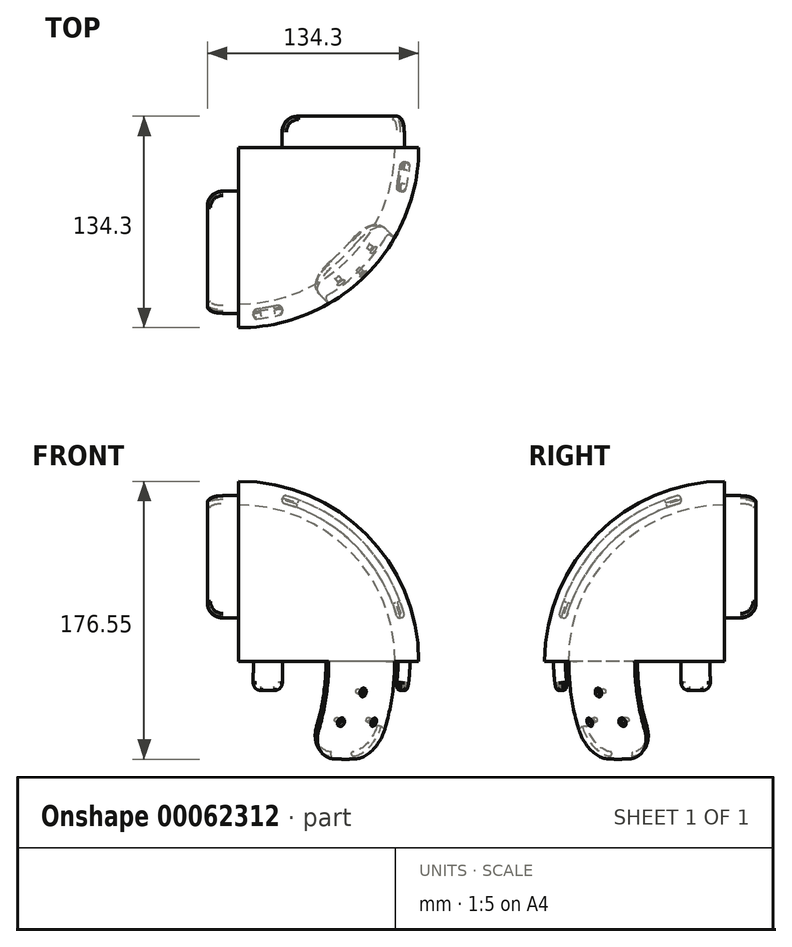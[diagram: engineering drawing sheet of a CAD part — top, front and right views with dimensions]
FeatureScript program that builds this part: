
annotation { "Feature Type Name" : "Feature", "Feature Type Description" : "" }
export const myFeature = defineFeature(function(context is Context, id is Id, definition is map)
    precondition{}
    {
        {
            var Q0;
            Q0=qCreatedBy(makeId("Right.planeOp"),FACE);
            var sketch = newSketch(context, id + "F0", { "sketchPlane" : qUnion([Q0])});
            skArc(sketch, "E0", {"start": v(0, 114.3) * mm, "mid": v(-80.82, 80.82) * mm, "end": v(-114.3, 0) * mm});
            skArc(sketch, "E1", {"start": v(0, 99.3) * mm, "mid": v(-70.22, 70.22) * mm, "end": v(-99.3, 0) * mm});
            skLineSegment(sketch, "E2", {"start": v(0, 99.3) * mm, "end": v(0, 114.3) * mm});
            skLineSegment(sketch, "E3", {"start": v(-99.3, 0) * mm, "end": v(-114.3, 0) * mm});
            skSolve(sketch);
        }
        {
            var Q0;
            Q0=makeQuery(id+"F0.imprint","IMPRINT",FACE,{"disambiguationData":[TD([[makeQuery(id+"F0.imprint","IMPRINT",EDGE,{"derivedFrom":sQuery(id+"F0.wireOp",EDGE,"E0")}),1.0]])]});
            var Q1;
            Q1=sQuery(id+"F0.wireOp",EDGE,"E2");
            revolve(context, id + "F1", {"entities" : qUnion([Q0]), "axis" : qUnion([Q1]), "revolveType" : RevolveType.ONE_DIRECTION, "angle" : 90 * degree});
        }
        {
            var Q0;
            Q0=makeQuery(id+"F1.opRevolve","CAP_FACE",FACE,{"disambiguationData":[OSD([sQuery(id+"F0.wireOp",EDGE,"E0"),sQuery(id+"F0.wireOp",EDGE,"E1"),sQuery(id+"F0.wireOp",EDGE,"E2"),sQuery(id+"F0.wireOp",EDGE,"E3")])],"isStart":false});
            var sketch = newSketch(context, id + "F2", { "sketchPlane" : qUnion([Q0])});
            skArc(sketch, "E4", {"start": v(-28.29, 105.58) * mm, "mid": v(-77.29, 77.29) * mm, "end": v(-105.58, 28.29) * mm});
            skArc(sketch, "E5", {"start": v(-27, 100.75) * mm, "mid": v(-73.75, 73.75) * mm, "end": v(-100.75, 27) * mm});
            skLineSegment(sketch, "E6", {"start": v(-27, 100.75) * mm, "end": v(-28.29, 105.58) * mm});
            skLineSegment(sketch, "E7", {"start": v(-100.75, 27) * mm, "end": v(-105.58, 28.29) * mm});
            skSolve(sketch);
        }
        {
            var Q0;
            Q0=makeQuery(id+"F2.imprint","IMPRINT",FACE,{"disambiguationData":[TD([[makeQuery(id+"F2.imprint","IMPRINT",EDGE,{"derivedFrom":sQuery(id+"F2.wireOp",EDGE,"E4")}),1.0]])]});
            extrude(context, id + "F3", {"entities" : qUnion([Q0]), "operationType" : NewBodyOperationType.ADD, "depth" : 20 * mm});
        }
        {
            var Q0;
            Q0=makeQuery(id+"F0.imprint","IMPRINT",FACE,{"disambiguationData":[TD([[makeQuery(id+"F0.imprint","IMPRINT",EDGE,{"derivedFrom":sQuery(id+"F0.wireOp",EDGE,"E0")}),1.0]])]});
            var sketch = newSketch(context, id + "F4", { "sketchPlane" : qUnion([Q0])});
            skArc(sketch, "E8.0", {"start": v(-27, 100.75) * mm, "mid": v(-73.75, 73.75) * mm, "end": v(-100.75, 27) * mm});
            skArc(sketch, "E9.0", {"start": v(-28.29, 105.58) * mm, "mid": v(-77.29, 77.29) * mm, "end": v(-105.58, 28.29) * mm});
            skLineSegment(sketch, "E10", {"start": v(-27, 100.75) * mm, "end": v(-28.29, 105.58) * mm});
            skLineSegment(sketch, "E11", {"start": v(-100.75, 27) * mm, "end": v(-105.58, 28.29) * mm});
            skSolve(sketch);
        }
        {
            var Q0;
            Q0=makeQuery(id+"F4.imprint","IMPRINT",FACE,{"disambiguationData":[TD([[makeQuery(id+"F4.imprint","IMPRINT",EDGE,{"derivedFrom":sQuery(id+"F4.wireOp",EDGE,"E8.0")}),-1.0]])]});
            extrude(context, id + "F5", {"entities" : qUnion([Q0]), "operationType" : NewBodyOperationType.ADD, "oppositeDirection" : true, "depth" : 20 * mm});
        }
        {
            var Q0;
            Q0=makeQuery(id+"F3.opExtrude","CAP_EDGE",EDGE,{"disambiguationData":[OSD([sQuery(id+"F2.wireOp",EDGE,"E7")])],"isStart":false});
            var Q1;
            Q1=makeQuery(id+"F3.opExtrude","CAP_EDGE",EDGE,{"disambiguationData":[OSD([sQuery(id+"F2.wireOp",EDGE,"E6")])],"isStart":false});
            var Q2;
            Q2=makeQuery(id+"F5.opExtrude","CAP_EDGE",EDGE,{"disambiguationData":[OSD([sQuery(id+"F4.wireOp",EDGE,"E10")])],"isStart":false});
            var Q3;
            Q3=makeQuery(id+"F5.opExtrude","CAP_EDGE",EDGE,{"disambiguationData":[OSD([sQuery(id+"F4.wireOp",EDGE,"E11")])],"isStart":false});
            fillet(context, id + "F6", {"entities" : qUnion([Q0, Q1, Q2, Q3]), "radius" : 10 * mm, "tangentPropagation" : true, "allowEdgeOverflow" : false});
        }
        {
            var Q0;
            Q0=makeQuery(id+"F1.opRevolve","SWEPT_FACE",FACE,{"disambiguationData":[OSD([sQuery(id+"F0.wireOp",EDGE,"E3")])]});
            var sketch = newSketch(context, id + "F7", { "sketchPlane" : qUnion([Q0])});
            skArc(sketch, "E12", {"start": v(98.99, 57.15) * mm, "mid": v(80.82, 80.82) * mm, "end": v(57.15, 98.99) * mm});
            skArc(sketch, "E13", {"start": v(94.66, 54.65) * mm, "mid": v(77.29, 77.29) * mm, "end": v(54.65, 94.66) * mm});
            skLineSegment(sketch, "E14", {"start": v(54.65, 94.66) * mm, "end": v(57.15, 98.99) * mm});
            skLineSegment(sketch, "E15", {"start": v(94.66, 54.65) * mm, "end": v(98.99, 57.15) * mm});
            skSolve(sketch);
        }
        {
            var Q0;
            Q0=qCreatedBy(makeId("Top.planeOp"),FACE);
            var sketch = newSketch(context, id + "F8", { "sketchPlane" : qUnion([Q0])});
            skLineSegment(sketch, "E16", {"start": v(0, 0) * mm, "end": v(-75, -75) * mm});
            skLineSegment(sketch, "E17", {"start": v(0, 0) * mm, "end": v(110.33, -110.33) * mm, "construction": true});
            skSolve(sketch);
        }
        {
            var Q0;
            Q0=makeQuery(id+"F7.imprint","IMPRINT",FACE,{"disambiguationData":[TD([[makeQuery(id+"F7.imprint","IMPRINT",EDGE,{"derivedFrom":sQuery(id+"F7.wireOp",EDGE,"E12")}),1.0]])]});
            var Q1;
            Q1=sQuery(id+"F8.wireOp",EDGE,"E16");
            revolve(context, id + "F9", {"operationType" : NewBodyOperationType.ADD, "entities" : qUnion([Q0]), "axis" : qUnion([Q1]), "revolveType" : RevolveType.ONE_DIRECTION, "oppositeDirection" : true, "angle" : 33 * degree});
        }
        {
            var Q0;
            Q0=makeQuery(id+"F5.boolean.opBoolean","MERGE",FACE,{"derivedFrom":[makeQuery(id+"F3.boolean.opBoolean","MERGE",FACE,{"derivedFrom":[makeQuery(id+"F1.opRevolve","SWEPT_FACE",FACE,{"disambiguationData":[OSD([sQuery(id+"F0.wireOp",EDGE,"E3")])]}),makeQuery(id+"F3.opExtrude","SWEPT_FACE",FACE,{"disambiguationData":[OSD([sQuery(id+"F2.wireOp",EDGE,"tj54Cu89-9J1S-AJKw-QeEM-ljXHSpR1f2pj")])]})]}),makeQuery(id+"F5.opExtrude","SWEPT_FACE",FACE,{"disambiguationData":[OSD([sQuery(id+"F4.wireOp",EDGE,"EMUQLBOC-9Rso-lLbz-JRUg-i4oPmn0DbPj1")])]})]});
            var sketch = newSketch(context, id + "F10", { "sketchPlane" : qUnion([Q0])});
            skArc(sketch, "E18", {"start": v(103.9, 9.1) * mm, "mid": v(102.72, 18.11) * mm, "end": v(100.75, 27) * mm});
            skArc(sketch, "E19", {"start": v(108.88, 9.53) * mm, "mid": v(107.64, 18.98) * mm, "end": v(105.58, 28.29) * mm});
            skLineSegment(sketch, "E20", {"start": v(9.1, 103.9) * mm, "end": v(9.53, 108.88) * mm});
            skLineSegment(sketch, "E21", {"start": v(27, 100.75) * mm, "end": v(28.29, 105.58) * mm});
            skLineSegment(sketch, "E22", {"start": v(100.75, 27) * mm, "end": v(105.58, 28.29) * mm});
            skLineSegment(sketch, "E23", {"start": v(103.9, 9.1) * mm, "end": v(108.88, 9.53) * mm});
            skArc(sketch, "E24.trimOffspring", {"start": v(27, 100.75) * mm, "mid": v(18.11, 102.72) * mm, "end": v(9.1, 103.9) * mm});
            skArc(sketch, "E25.trimOffspring", {"start": v(28.29, 105.58) * mm, "mid": v(18.98, 107.64) * mm, "end": v(9.53, 108.88) * mm});
            skSolve(sketch);
        }
        {
            var Q0;
            Q0=qCreatedBy(makeId("Top.planeOp"),FACE);
            var sketch = newSketch(context, id + "F11", { "sketchPlane" : qUnion([Q0])});
            skLineSegment(sketch, "E26", {"start": v(0, 0) * mm, "end": v(-66.83, -11.78) * mm});
            skLineSegment(sketch, "E27", {"start": v(0, 0) * mm, "end": v(-14.4, -81.7) * mm});
            skSolve(sketch);
        }
        {
            var Q0;
            Q0=makeQuery(id+"F10.imprint","IMPRINT",FACE,{"disambiguationData":[TD([[makeQuery(id+"F10.imprint","IMPRINT",EDGE,{"derivedFrom":sQuery(id+"F10.wireOp",EDGE,"E20")}),-1.0]])]});
            var Q1;
            Q1=sQuery(id+"F11.wireOp",EDGE,"E26");
            revolve(context, id + "F12", {"operationType" : NewBodyOperationType.ADD, "entities" : qUnion([Q0]), "axis" : qUnion([Q1]), "revolveType" : RevolveType.ONE_DIRECTION, "oppositeDirection" : true, "angle" : 10 * degree});
        }
        {
            var Q0;
            Q0=makeQuery(id+"F10.imprint","IMPRINT",FACE,{"disambiguationData":[TD([[makeQuery(id+"F10.imprint","IMPRINT",EDGE,{"derivedFrom":sQuery(id+"F10.wireOp",EDGE,"E18")}),-1.0]])]});
            var Q1;
            Q1=sQuery(id+"F11.wireOp",EDGE,"E27");
            revolve(context, id + "F13", {"operationType" : NewBodyOperationType.ADD, "entities" : qUnion([Q0]), "axis" : qUnion([Q1]), "revolveType" : RevolveType.ONE_DIRECTION, "oppositeDirection" : true, "angle" : 10 * degree});
        }
        {
            var Q0;
            Q0=qCreatedBy(makeId("Front.planeOp"),FACE);
            var Q1;
            Q1=sQuery(id+"F8.wireOp",EDGE,"E16");
            cPlane(context, id + "F14", {"entities" : qUnion([Q0, Q1]), "cplaneType" : CPlaneType.LINE_ANGLE, "offset" : 10 * mm, "angle" : 0 * degree, "width" : 150 * mm, "height" : 150 * mm});
        }
        {
            var Q0;
            Q0=qCreatedBy(id+"F14.planeOp",FACE);
            cPlane(context, id + "F15", {"entities" : qUnion([Q0]), "cplaneType" : CPlaneType.OFFSET, "offset" : 114.3 * mm, "oppositeDirection" : true, "width" : 150 * mm, "height" : 150 * mm});
        }
        {
            var Q0;
            Q0=qCreatedBy(makeId("Top.planeOp"),FACE);
            var Q1;
            Q1=sQuery(id+"F8.wireOp",EDGE,"E16");
            cPlane(context, id + "F16", {"entities" : qUnion([Q0, Q1]), "cplaneType" : CPlaneType.LINE_ANGLE, "offset" : 150 * mm, "angle" : 340 * degree, "width" : 150 * mm, "height" : 150 * mm});
        }
        {
            var Q0;
            Q0=qCreatedBy(makeId("Top.planeOp"),FACE);
            var Q1;
            Q1=sQuery(id+"F8.wireOp",EDGE,"E16");
            cPlane(context, id + "F17", {"entities" : qUnion([Q0, Q1]), "cplaneType" : CPlaneType.LINE_ANGLE, "offset" : 150 * mm, "angle" : 350 * degree, "width" : 150 * mm, "height" : 150 * mm});
        }
        {
            var Q0;
            Q0=qCreatedBy(id+"F16.planeOp",FACE);
            var sketch = newSketch(context, id + "F18", { "sketchPlane" : qUnion([Q0])});
            skArc(sketch, "E28", {"start": v(88.32, 72.56) * mm, "mid": v(78.27, 83.3) * mm, "end": v(66.93, 92.65) * mm});
            skLineSegment(sketch, "E29", {"start": v(0, 0) * mm, "end": v(66.93, 92.65) * mm, "construction": true});
            skLineSegment(sketch, "E30", {"start": v(0, 0) * mm, "end": v(88.32, 72.56) * mm, "construction": true});
            skLineSegment(sketch, "E31", {"start": v(84, 80.32) * mm, "end": v(66.93, 92.65) * mm, "construction": true});
            skLineSegment(sketch, "E32", {"start": v(88.32, 72.56) * mm, "end": v(103.67, 53.87) * mm, "construction": true});
            skSolve(sketch);
        }
        {
            var Q0;
            Q0=qCreatedBy(id+"F17.planeOp",FACE);
            var sketch = newSketch(context, id + "F19", { "sketchPlane" : qUnion([Q0])});
            skLineSegment(sketch, "E33", {"start": v(0, 0) * mm, "end": v(79.58, 82.05) * mm, "construction": true});
            skLineSegment(sketch, "E34", {"start": v(79.58, 82.05) * mm, "end": v(93.93, 68.13) * mm, "construction": true});
            skSolve(sketch);
        }
        {
            var Q0;
            Q0=sQuery(id+"F18.wireOp",EDGE,"E31");
            var Q1;
            Q1=sQuery(id+"F18.wireOp",EDGE,"E29");
            cPlane(context, id + "F20", {"entities" : qUnion([Q0, Q1]), "cplaneType" : CPlaneType.LINE_ANGLE, "offset" : 150 * mm, "angle" : 90 * degree, "width" : 150 * mm, "height" : 150 * mm});
        }
        {
            var Q0;
            Q0=sQuery(id+"F18.wireOp",EDGE,"E32");
            var Q1;
            Q1=sQuery(id+"F18.wireOp",EDGE,"E30");
            cPlane(context, id + "F21", {"entities" : qUnion([Q0, Q1]), "cplaneType" : CPlaneType.LINE_ANGLE, "offset" : 150 * mm, "angle" : 90 * degree, "width" : 150 * mm, "height" : 150 * mm});
        }
        {
            var Q0;
            Q0=sQuery(id+"F19.wireOp",EDGE,"E34");
            var Q1;
            Q1=sQuery(id+"F19.wireOp",EDGE,"E33");
            cPlane(context, id + "F22", {"entities" : qUnion([Q0, Q1]), "cplaneType" : CPlaneType.LINE_ANGLE, "offset" : 150 * mm, "angle" : 90 * degree, "width" : 150 * mm, "height" : 150 * mm});
        }
        {
            var Q0;
            Q0=qCreatedBy(id+"F20.planeOp",FACE);
            var sketch = newSketch(context, id + "F23", { "sketchPlane" : qUnion([Q0])});
            skPoint(sketch, "E35", {"position": v(0, 0) * mm});
            skSolve(sketch);
        }
        {
            var Q0;
            Q0=qCreatedBy(id+"F21.planeOp",FACE);
            var sketch = newSketch(context, id + "F24", { "sketchPlane" : qUnion([Q0])});
            skPoint(sketch, "E36", {"position": v(0, 0) * mm});
            skSolve(sketch);
        }
        {
            var Q0;
            Q0=qCreatedBy(id+"F22.planeOp",FACE);
            var sketch = newSketch(context, id + "F25", { "sketchPlane" : qUnion([Q0])});
            skPoint(sketch, "E37", {"position": v(0, 0) * mm});
            skSolve(sketch);
        }
        {
            var Q0;
            Q0=sQuery(id+"F23.wireOp",VERTEX,"E35");
            var Q1;
            Q1=sQuery(id+"F24.wireOp",VERTEX,"E36");
            var Q2;
            Q2=sQuery(id+"F25.wireOp",VERTEX,"E37");
            var Q3;
            Q3=makeQuery(id+"F1.opRevolve","SWEPT_BODY",BODY,{"disambiguationData":[OSD([sQuery(id+"F0.wireOp",EDGE,"E0"),sQuery(id+"F0.wireOp",EDGE,"E1"),sQuery(id+"F0.wireOp",EDGE,"E2"),sQuery(id+"F0.wireOp",EDGE,"E3")])]});
            hole(context, id + "F26", {"style" : HoleStyle.C_SINK, "holeDiameter" : 3 * mm, "cSinkDiameter" : 5.6 * mm, "endStyle" : HoleEndStyle.THROUGH, "oppositeDirection" : true, "locations" : qUnion([Q0, Q1, Q2]), "scope" : qUnion([Q3]), "cSinkAngle" : 90 * degree});
        }
        {
            var Q0;
            Q0=makeQuery(id+"F9.opRevolve","CAP_EDGE",EDGE,{"disambiguationData":[OSD([sQuery(id+"F7.wireOp",EDGE,"E15")])],"isStart":false});
            var Q1;
            Q1=makeQuery(id+"F9.opRevolve","CAP_EDGE",EDGE,{"disambiguationData":[OSD([sQuery(id+"F7.wireOp",EDGE,"E14")])],"isStart":false});
            fillet(context, id + "F27", {"entities" : qUnion([Q0, Q1]), "radius" : 20 * mm, "tangentPropagation" : true, "allowEdgeOverflow" : false});
        }
        {
            var Q0;
            Q0=makeQuery(id+"F9.opRevolve","SWEPT_EDGE",EDGE,{"disambiguationData":[OSD([sQuery(id+"F7.wireOp",EDGE,"E13"),sQuery(id+"F7.wireOp",EDGE,"E14")])]});
            fillet(context, id + "F28", {"entities" : qUnion([Q0]), "radius" : 2 * mm, "tangentPropagation" : true, "allowEdgeOverflow" : false});
        }
        {
            var Q0;
            Q0=makeQuery(id+"F12.opRevolve","CAP_EDGE",EDGE,{"disambiguationData":[OSD([sQuery(id+"F10.wireOp",EDGE,"E20")])],"isStart":false});
            var Q1;
            Q1=makeQuery(id+"F12.opRevolve","CAP_EDGE",EDGE,{"disambiguationData":[OSD([sQuery(id+"F10.wireOp",EDGE,"E21")])],"isStart":false});
            var Q2;
            Q2=makeQuery(id+"F13.opRevolve","CAP_EDGE",EDGE,{"disambiguationData":[OSD([sQuery(id+"F10.wireOp",EDGE,"E23")])],"isStart":false});
            var Q3;
            Q3=makeQuery(id+"F13.opRevolve","CAP_EDGE",EDGE,{"disambiguationData":[OSD([sQuery(id+"F10.wireOp",EDGE,"E22")])],"isStart":false});
            fillet(context, id + "F29", {"entities" : qUnion([Q0, Q1, Q2, Q3]), "radius" : 5 * mm, "tangentPropagation" : true, "allowEdgeOverflow" : false});
        }
        {
            var Q0;
            Q0=makeQuery(id+"F5.opExtrude","CAP_EDGE",EDGE,{"disambiguationData":[OSD([sQuery(id+"F4.wireOp",EDGE,"E8.0")])],"isStart":false});
            var Q1;
            Q1=makeQuery(id+"F3.opExtrude","CAP_EDGE",EDGE,{"disambiguationData":[OSD([sQuery(id+"F2.wireOp",EDGE,"E5")])],"isStart":false});
            var Q2;
            Q2=makeQuery(id+"F3.opExtrude","CAP_EDGE",EDGE,{"disambiguationData":[OSD([sQuery(id+"F2.wireOp",EDGE,"E4")])],"isStart":false});
            var Q3;
            Q3=makeQuery(id+"F5.opExtrude","CAP_EDGE",EDGE,{"disambiguationData":[OSD([sQuery(id+"F4.wireOp",EDGE,"E9.0")])],"isStart":false});
            var Q4;
            Q4=makeQuery(id+"F12.opRevolve","CAP_EDGE",EDGE,{"disambiguationData":[OSD([sQuery(id+"F10.wireOp",EDGE,"E25.trimOffspring")])],"isStart":false});
            var Q5;
            Q5=makeQuery(id+"F12.opRevolve","SWEPT_EDGE",EDGE,{"disambiguationData":[OSD([sQuery(id+"F10.wireOp",EDGE,"E21"),sQuery(id+"F10.wireOp",EDGE,"E24.trimOffspring")])]});
            var Q6;
            Q6=makeQuery(id+"F13.opRevolve","CAP_EDGE",EDGE,{"disambiguationData":[OSD([sQuery(id+"F10.wireOp",EDGE,"E18")])],"isStart":false});
            var Q7;
            Q7=makeQuery(id+"F13.opRevolve","CAP_EDGE",EDGE,{"disambiguationData":[OSD([sQuery(id+"F10.wireOp",EDGE,"E19")])],"isStart":false});
            fillet(context, id + "F30", {"entities" : qUnion([Q0, Q1, Q2, Q3, Q4, Q5, Q6, Q7]), "radius" : 2 * mm, "tangentPropagation" : true, "allowEdgeOverflow" : false});
        }
    });
